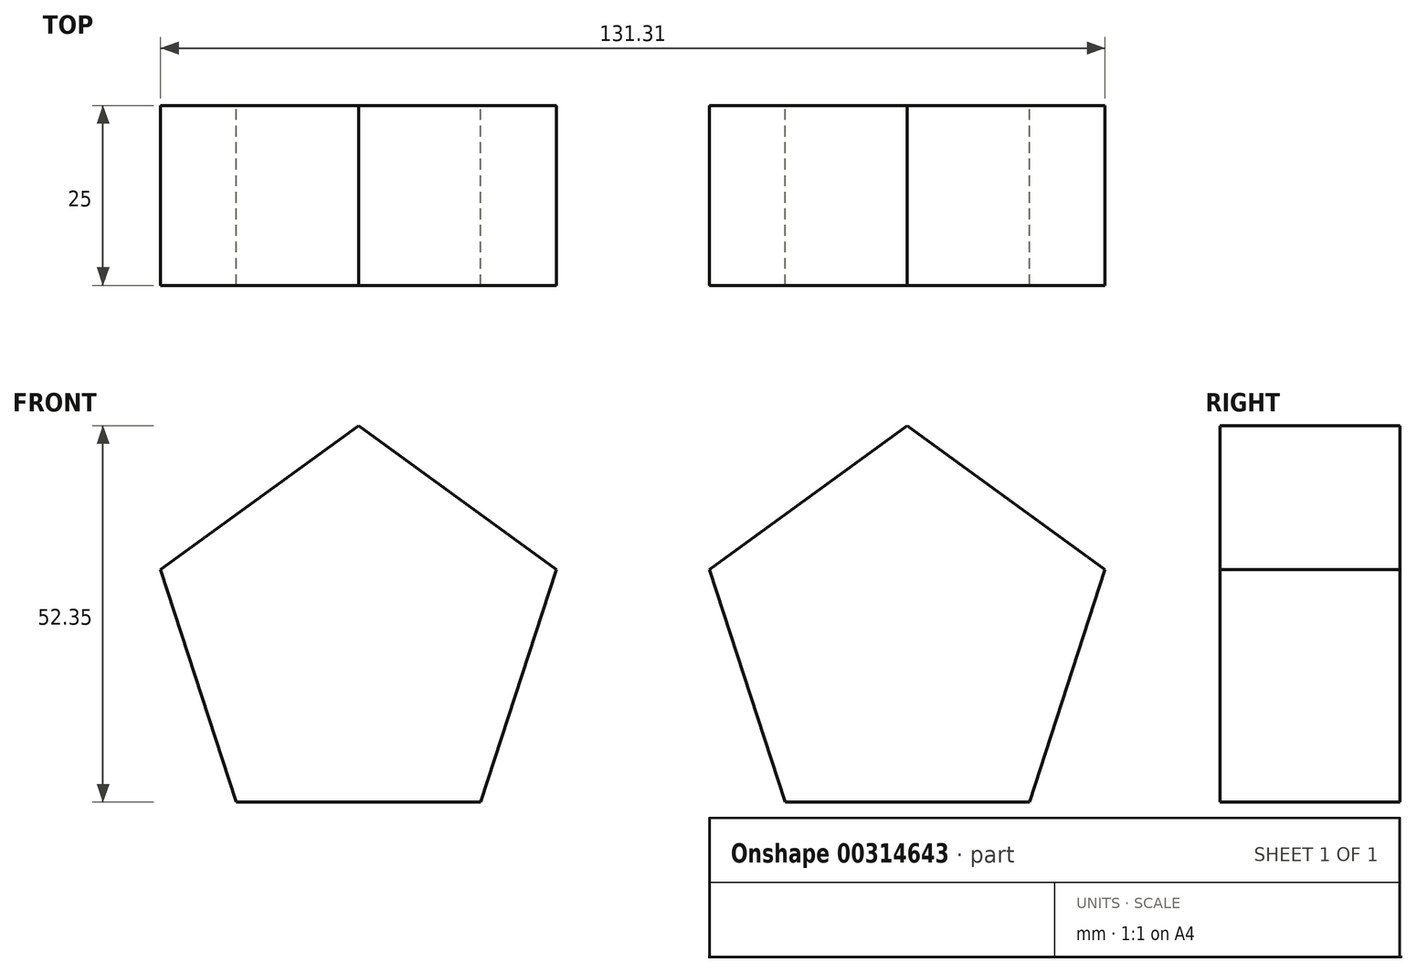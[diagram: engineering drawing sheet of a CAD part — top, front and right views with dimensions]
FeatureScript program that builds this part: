
annotation { "Feature Type Name" : "Feature", "Feature Type Description" : "" }
export const myFeature = defineFeature(function(context is Context, id is Id, definition is map)
    precondition{}
    {
        {
            var Q0;
            Q0=qCreatedBy(makeId("Front.planeOp"),FACE);
            var sketch = newSketch(context, id + "F0", { "sketchPlane" : qUnion([Q0])});
            skLineSegment(sketch, "E0.0", {"start": v(-27.3, -24.42) * mm, "end": v(-61.3, -24.42) * mm});
            skLineSegment(sketch, "E0.1", {"start": v(-61.3, -24.42) * mm, "end": v(-71.81, 7.91) * mm});
            skLineSegment(sketch, "E0.2", {"start": v(-71.81, 7.91) * mm, "end": v(-44.3, 27.9) * mm});
            skLineSegment(sketch, "E0.3", {"start": v(-44.3, 27.9) * mm, "end": v(-16.8, 7.91) * mm});
            skLineSegment(sketch, "E0.4", {"start": v(-16.8, 7.91) * mm, "end": v(-27.3, -24.42) * mm});
            skPoint(sketch, "E0.0.midPoint", {"position": v(-44.3, -24.42) * mm});
            skLineSegment(sketch, "E1", {"start": v(-44.3, 27.9) * mm, "end": v(-61.3, -24.42) * mm});
            skLineSegment(sketch, "E2", {"start": v(-61.3, -24.42) * mm, "end": v(-16.8, 7.91) * mm});
            skLineSegment(sketch, "E3", {"start": v(-16.8, 7.91) * mm, "end": v(-71.81, 7.91) * mm});
            skLineSegment(sketch, "E4", {"start": v(-71.81, 7.91) * mm, "end": v(-27.3, -24.42) * mm});
            skLineSegment(sketch, "E5", {"start": v(-27.3, -24.42) * mm, "end": v(-44.3, 27.9) * mm});
            skLineSegment(sketch, "E6", {"start": v(32, 27.9) * mm, "end": v(4.5, 7.9) * mm});
            skLineSegment(sketch, "E7", {"start": v(4.5, 7.9) * mm, "end": v(15.02, -24.45) * mm});
            skLineSegment(sketch, "E8", {"start": v(15.02, -24.45) * mm, "end": v(48.98, -24.45) * mm});
            skLineSegment(sketch, "E9", {"start": v(48.98, -24.45) * mm, "end": v(59.5, 7.9) * mm});
            skLineSegment(sketch, "E10", {"start": v(59.5, 7.9) * mm, "end": v(32, 27.9) * mm});
            skLineSegment(sketch, "E11", {"start": v(4.5, 7.9) * mm, "end": v(59.5, 7.9) * mm});
            skLineSegment(sketch, "E12", {"start": v(32, 27.9) * mm, "end": v(32, -24.45) * mm});
            skPoint(sketch, "E13", {"position": v(32, 7.9) * mm});
            skLineSegment(sketch, "E14", {"start": v(59.5, 7.9) * mm, "end": v(15.02, -24.45) * mm});
            skSolve(sketch);
        }
        {
            var Q0;
            Q0 = qSketchRegion(id + "F0", true);
            var Q1;
            {var subQ1=sQuery(id+"F0.wireOp",EDGE,"E1");var subQ5=sQuery(id+"F0.wireOp",EDGE,"E3");var subQ6=makeQuery(id+"F0.imprint","INTERSECT",VERTEX,{"derivedFrom":[subQ1,subQ5]});Q1=makeQuery(id+"F0.imprint","IMPRINT",FACE,{"disambiguationData":[TD([[makeQuery(id+"F0.imprint","IMPRINT",EDGE,{"disambiguationData":[TD([[subQ6,-1.0]])],"derivedFrom":subQ1}),1.0]])]});}
            extrude(context, id + "F1", {"entities" : qUnion([Q0, Q1]), "depth" : 25 * mm, "offsetDistance" : 25 * mm});
        }
    });
